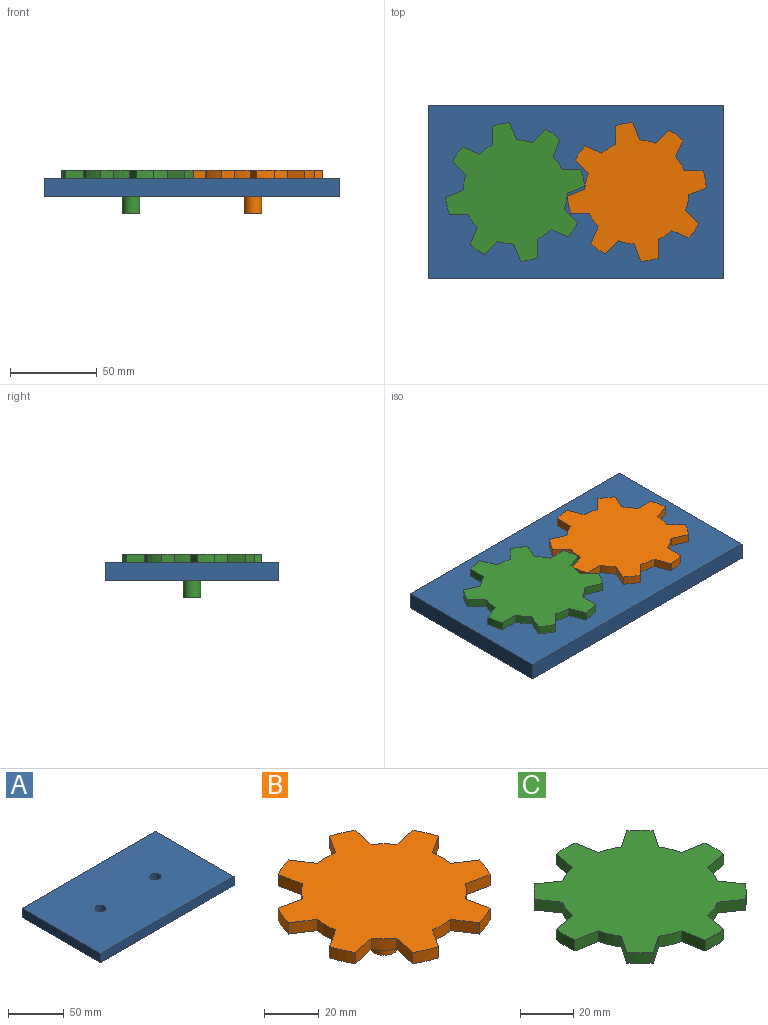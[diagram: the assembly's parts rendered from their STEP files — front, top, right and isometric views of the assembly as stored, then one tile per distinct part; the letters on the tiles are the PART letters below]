
ASSEMBLY  parts=3 mates=2
PART A: 8 faces, bbox 170x100x10 mm
  f0: plane 170x10mm, normal (0,-1,0), area 1700mm2, adj f1,f3,f4,f5
  f1: plane 100x10mm, normal (1,0,0), area 1000mm2, adj f0,f2,f4,f5
  f2: plane 170x10mm, normal (0,1,0), area 1700mm2, adj f1,f3,f4,f5
  f3: plane 100x10mm, normal (-1,0,0), area 1000mm2, adj f0,f2,f4,f5
  f4: plane 170x100mm, normal (0,0,-1), area 16842.9mm2, adj f0,f1,f2,f3,f6,f7
  f5: plane 170x100mm, normal (0,0,1), area 16842.9mm2, adj f0,f1,f2,f3,f6,f7
  f6: cylinder r=5mm len=10mm, axis (0,0,1), area 314.2mm2, adj f4,f5
  f7: cylinder r=5mm len=10mm, axis (0,0,1), area 314.2mm2, adj f4,f5
PART B: 36 faces, bbox 77.2x77.2x25 mm
  f0: plane 8.96x5.82mm, normal (0.54,0.84,0), area 53.4mm2, adj f1,f31,f32,f33
  f1: cylinder r=30mm len=9.44mm, axis (0,0,-1), area 47.4mm2, adj f0,f2,f32,f33
  f2: plane 8.96x5.82mm, normal (0.54,-0.84,0), area 53.4mm2, adj f1,f3,f32,f33
  f3: cylinder r=40mm len=9.28mm, axis (0,0,-1), area 50.4mm2, adj f2,f4,f32,f33
  f4: plane 10.45x5mm, normal (-0.21,0.98,0), area 53.4mm2, adj f3,f5,f32,f33
  f5: cylinder r=30mm len=6.68mm, axis (0,0,-1), area 47.4mm2, adj f4,f6,f32,f33
  f6: plane 10.45x5mm, normal (0.98,-0.21,0), area 53.4mm2, adj f5,f7,f32,f33
  f7: cylinder r=40mm len=9.28mm, axis (0,0,-1), area 50.4mm2, adj f6,f8,f32,f33
  f8: plane 8.96x5.82mm, normal (-0.84,0.54,0), area 53.4mm2, adj f7,f9,f32,f33
  f9: cylinder r=30mm len=9.44mm, axis (0,0,-1), area 47.4mm2, adj f8,f10,f32,f33
  f10: plane 8.96x5.82mm, normal (0.84,0.54,0), area 53.4mm2, adj f9,f11,f32,f33
  f11: cylinder r=40mm len=9.28mm, axis (0,0,-1), area 50.4mm2, adj f10,f12,f32,f33
  f12: plane 10.45x5mm, normal (-0.98,-0.21,0), area 53.4mm2, adj f11,f13,f32,f33
  f13: cylinder r=30mm len=6.68mm, axis (0,0,-1), area 47.4mm2, adj f12,f14,f32,f33
  f14: plane 10.45x5mm, normal (0.21,0.98,0), area 53.4mm2, adj f13,f15,f32,f33
  f15: cylinder r=40mm len=9.28mm, axis (0,0,-1), area 50.4mm2, adj f14,f16,f32,f33
  f16: plane 8.96x5.82mm, normal (-0.54,-0.84,0), area 53.4mm2, adj f15,f17,f32,f33
  f17: cylinder r=30mm len=9.44mm, axis (0,0,-1), area 47.4mm2, adj f16,f18,f32,f33
  f18: plane 8.96x5.82mm, normal (-0.54,0.84,0), area 53.4mm2, adj f17,f19,f32,f33
  f19: cylinder r=40mm len=9.28mm, axis (0,0,-1), area 50.4mm2, adj f18,f20,f32,f33
  f20: plane 10.45x5mm, normal (0.21,-0.98,0), area 53.4mm2, adj f19,f21,f32,f33
  f21: cylinder r=30mm len=6.68mm, axis (0,0,-1), area 47.4mm2, adj f20,f22,f32,f33
  f22: plane 10.45x5mm, normal (-0.98,0.21,0), area 53.4mm2, adj f21,f23,f32,f33
  f23: cylinder r=40mm len=9.28mm, axis (0,0,-1), area 50.4mm2, adj f22,f24,f32,f33
  f24: plane 8.96x5.82mm, normal (0.84,-0.54,0), area 53.4mm2, adj f23,f25,f32,f33
  f25: cylinder r=30mm len=9.44mm, axis (0,0,-1), area 47.4mm2, adj f24,f26,f32,f33
  f26: plane 8.96x5.82mm, normal (-0.84,-0.54,0), area 53.4mm2, adj f25,f27,f32,f33
  f27: cylinder r=40mm len=9.28mm, axis (0,0,-1), area 50.4mm2, adj f26,f28,f32,f33
  f28: plane 10.45x5mm, normal (0.98,0.21,0), area 53.4mm2, adj f27,f29,f32,f33
  f29: cylinder r=30mm len=6.68mm, axis (0,0,-1), area 47.4mm2, adj f28,f30,f32,f33
  f30: plane 10.45x5mm, normal (-0.21,-0.98,0), area 53.4mm2, adj f29,f31,f32,f33
  f31: cylinder r=40mm len=9.28mm, axis (0,0,-1), area 50.4mm2, adj f0,f30,f32,f33
  f32: plane 77.17x77.17mm, normal (0,0,1), area 3791.5mm2, adj f0,f1,f2,f3,f4,f5,f6,f7
  f33: plane 77.17x77.17mm, normal (0,0,-1), area 3713mm2, adj f0,f1,f2,f3,f4,f5,f6,f7
  f34: cylinder r=5mm len=20mm, axis (0,0,1), area 628.3mm2, adj f33,f35
  f35: plane 10x10mm, normal (0,0,-1), area 78.5mm2, adj f34
PART C: 36 faces, bbox 80x80x25 mm
  f0: plane 8.81x6.05mm, normal (0.82,0.57,0), area 53.4mm2, adj f1,f31,f32,f33
  f1: cylinder r=30mm len=8.72mm, axis (0,0,-1), area 47.4mm2, adj f0,f2,f32,f33
  f2: plane 10.51x5mm, normal (0.18,-0.98,0), area 53.4mm2, adj f1,f3,f32,f33
  f3: cylinder r=40mm len=10.05mm, axis (0,0,-1), area 50.4mm2, adj f2,f4,f32,f33
  f4: plane 10.51x5mm, normal (0.18,0.98,0), area 53.4mm2, adj f3,f5,f32,f33
  f5: cylinder r=30mm len=8.72mm, axis (0,0,-1), area 47.4mm2, adj f4,f6,f32,f33
  f6: plane 8.81x6.05mm, normal (0.82,-0.57,0), area 53.4mm2, adj f5,f7,f32,f33
  f7: cylinder r=40mm len=7.1mm, axis (0,0,-1), area 50.4mm2, adj f6,f8,f32,f33
  f8: plane 8.81x6.05mm, normal (-0.57,0.82,0), area 53.4mm2, adj f7,f9,f32,f33
  f9: cylinder r=30mm len=8.72mm, axis (0,0,-1), area 47.4mm2, adj f8,f10,f32,f33
  f10: plane 10.51x5mm, normal (0.98,0.18,0), area 53.4mm2, adj f9,f11,f32,f33
  f11: cylinder r=40mm len=10.05mm, axis (0,0,-1), area 50.4mm2, adj f10,f12,f32,f33
  f12: plane 10.51x5mm, normal (-0.98,0.18,0), area 53.4mm2, adj f11,f13,f32,f33
  f13: cylinder r=30mm len=8.72mm, axis (0,0,-1), area 47.4mm2, adj f12,f14,f32,f33
  f14: plane 8.81x6.05mm, normal (0.57,0.82,0), area 53.4mm2, adj f13,f15,f32,f33
  f15: cylinder r=40mm len=7.1mm, axis (0,0,-1), area 50.4mm2, adj f14,f16,f32,f33
  f16: plane 8.81x6.05mm, normal (-0.82,-0.57,0), area 53.4mm2, adj f15,f17,f32,f33
  f17: cylinder r=30mm len=8.72mm, axis (0,0,-1), area 47.4mm2, adj f16,f18,f32,f33
  f18: plane 10.51x5mm, normal (-0.18,0.98,0), area 53.4mm2, adj f17,f19,f32,f33
  f19: cylinder r=40mm len=10.05mm, axis (0,0,-1), area 50.4mm2, adj f18,f20,f32,f33
  f20: plane 10.51x5mm, normal (-0.18,-0.98,0), area 53.4mm2, adj f19,f21,f32,f33
  f21: cylinder r=30mm len=8.72mm, axis (0,0,-1), area 47.4mm2, adj f20,f22,f32,f33
  f22: plane 8.81x6.05mm, normal (-0.82,0.57,0), area 53.4mm2, adj f21,f23,f32,f33
  f23: cylinder r=40mm len=7.1mm, axis (0,0,-1), area 50.4mm2, adj f22,f24,f32,f33
  f24: plane 8.81x6.05mm, normal (0.57,-0.82,0), area 53.4mm2, adj f23,f25,f32,f33
  f25: cylinder r=30mm len=8.72mm, axis (0,0,-1), area 47.4mm2, adj f24,f26,f32,f33
  f26: plane 10.51x5mm, normal (-0.98,-0.18,0), area 53.4mm2, adj f25,f27,f32,f33
  f27: cylinder r=40mm len=10.05mm, axis (0,0,-1), area 50.4mm2, adj f26,f28,f32,f33
  f28: plane 10.51x5mm, normal (0.98,-0.18,0), area 53.4mm2, adj f27,f29,f32,f33
  f29: cylinder r=30mm len=8.72mm, axis (0,0,-1), area 47.4mm2, adj f28,f30,f32,f33
  f30: plane 8.81x6.05mm, normal (-0.57,-0.82,0), area 53.4mm2, adj f29,f31,f32,f33
  f31: cylinder r=40mm len=7.1mm, axis (0,0,-1), area 50.4mm2, adj f0,f30,f32,f33
  f32: plane 80x80mm, normal (0,0,1), area 3791.5mm2, adj f0,f1,f2,f3,f4,f5,f6,f7
  f33: plane 80x80mm, normal (0,0,-1), area 3713mm2, adj f0,f1,f2,f3,f4,f5,f6,f7
  f34: cylinder r=5mm len=20mm, axis (0,0,1), area 628.3mm2, adj f33,f35
  f35: plane 10x10mm, normal (0,0,-1), area 78.5mm2, adj f34
PLACE A t=(-84.18,29.81,8.46)mm fixed
PLACE B rot(axis=(0,0,-1),56.9deg) t=(-52.4,88.45,8.46)mm
PLACE C rot(axis=(0,0,1),56.9deg) t=(-84.18,29.81,8.46)mm
MATE revolute A.f7 <-> B.f34  axis (0,0,1) through (-14.18,29.81,8.46)mm
MATE revolute A.f6 <-> C.f34  axis (0,0,1) through (-84.18,29.81,8.46)mm
